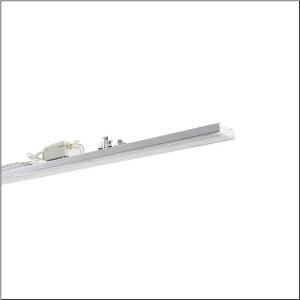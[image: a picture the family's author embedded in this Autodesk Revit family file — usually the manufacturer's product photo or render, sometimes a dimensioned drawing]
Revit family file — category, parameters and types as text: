
# Revit family: licross_21_recessed_mo_52tl1edv4e5g
name_source: partatom
category: Lighting Fixtures
units: mm (PartAtom-declared; Revit-internal decimal feet)

## family parameters
Cut with Voids When Loaded = No
Host = Face
Light Source = No
Part Type = Normal
Room Calculation Point = No
Round Connector Dimension = Use Diameter
Shared = No

## types (1)
- --- (1 x LED, 14910 lm, 85.3 W, 4000K)
    Apparent Load = 85 VA
    CIE Flux Codes = 85 95 99 100 100
    Color Rendering = 80
    Color Temperature = 4000K
    Default Elevation = 1800 mm
    Description = Licross 21 Recessed MO, luminaire insert, of sheet steel, galvanised, coil coated, white, length: 2.250mm, width: 66mm, height: 67mm, LED rated luminous flux: 14.910lm, light colour: 840, SDCM (Standard Deviation of Colour Matching)MacAdam ≤ 3 SDCM (initial), control gear: DALI 2, with plug, 5-pole, with phase selection, mains connection: 220..240V, AC, 50/60Hz, rated input power: 85W, internal wiring halogen-free, primary light control with lens, of plastic, primary optical cover: cover, of PMMA, light emission: direct distribution, primary light characteristic: symmetric, protection rating (complete): IP40, insulation class (complete): insulation class I (protective earthing), certification: CE, ENEC, VDE, UKCA, protection symbol: D if used in an environment without relevant dust loads with corresponding accessories, impact resistance: IK06, permissible ambient temperature for indoor applications: -25..+35°C, corresponds to IFS (International Featured Standards) requirements for safety and quality in the food industry, reducing of maximum allowable ambient temperature of 5°C with ceiling mounting, LABS conformity tested according to VDMA 24364:2018-05, The light source and the operating device comply with the requirements of the Ecodesign Regulation (EU) 2019/2020 and are replaceable in accordance with this regulation, packaging unit: 1 piece
    Height = 58 mm
    Lamp = 1 x LED
    Lamp Light Flux = 14910 lm
    Lamp Power = 85.3 W
    Lamp count = 1
    Length = 2250 mm
    Luminous efficacy = 175 lm/W
    Manufacturer = Siteco
    ModVariant = No
    Model = 52TL1EDV4E5G
    Mounting Place = Ceiling
    Mounting Type = Pendant
    Number of Poles = 1
    OnlyDefault = Yes
    Power Factor = 1
    Product Name = Licross 21 Recessed MO
    Product group = luminaire insert | ceiling pendant
    ProductGroupID = 901
    Protection Class = Protection class I
    Protection Degree = IP 40
    RLX_Detail_Level = 1
    RLX_Emergency_Light_Flux = 0 lm
    RLX_Emergency_Type = 0
    RLX_Emergency_Type_DB = No
    RlxData = <blob elided: 29849 chars, md5=0f2eda09>
    Socket = socket
    Standby Power = 0 W
    System Light Flux = 14910 lm
    System Power = 85 W
    Type Comments = factory setting: luminous flux: 100 % | dim-lin: 254 | 390 mA
    Type Image = l_1296930.jpg
    URL = http://relux.com
    VarID = @adj_127313
    Voltage = 0 V
    Weight = 0.00 kg
    Width = 66 mm

## geometry (parser evidence)
native form markers: Blend x4, Sweep x11
no freeform markers — native parametric forms only
